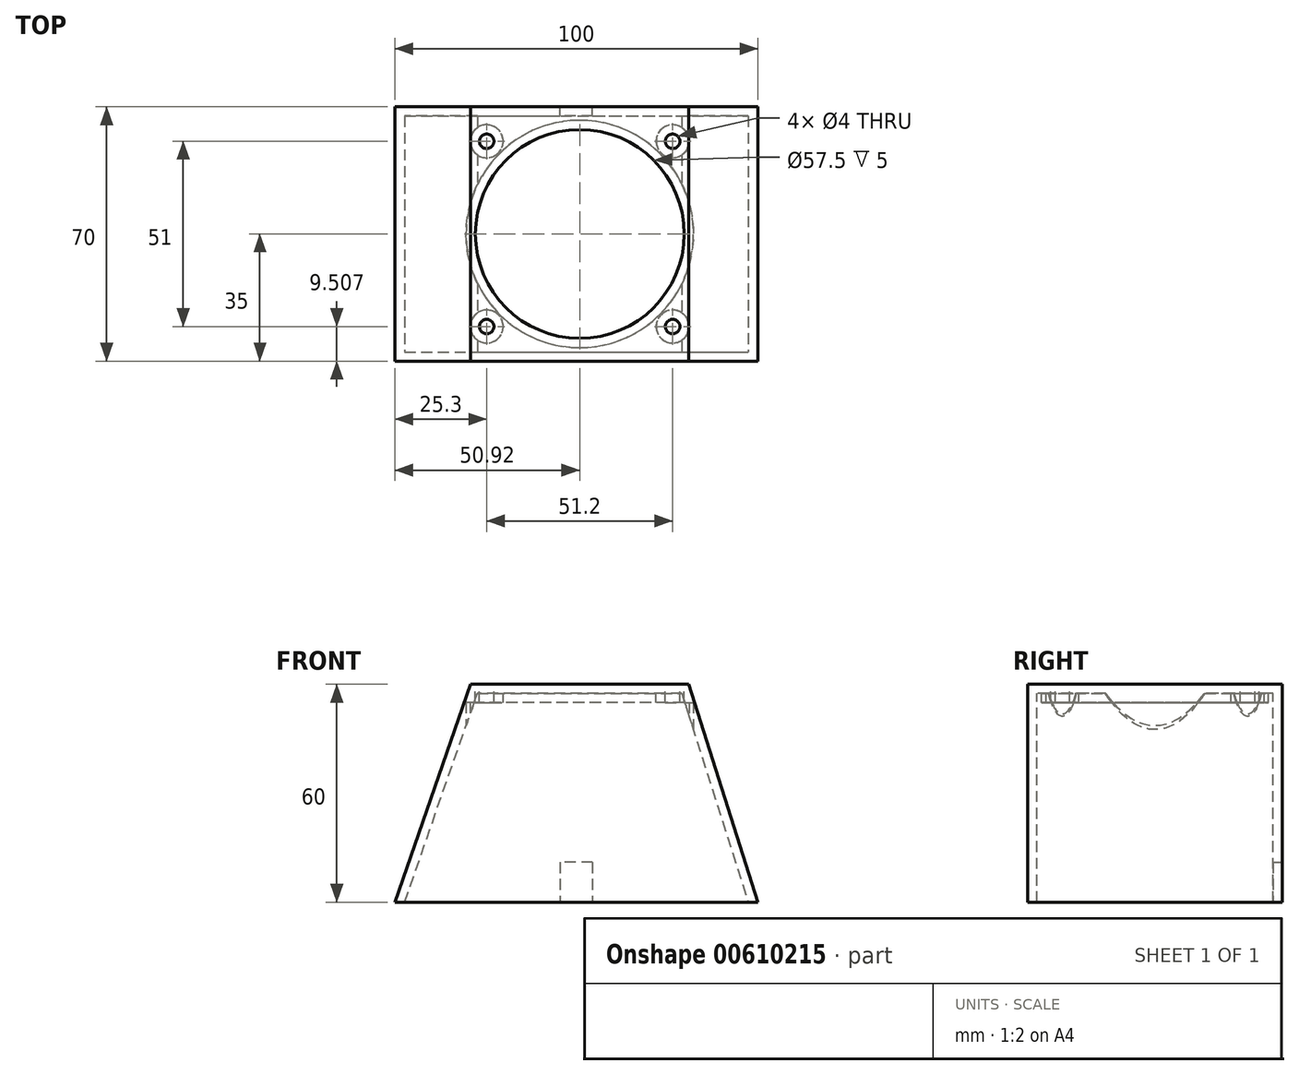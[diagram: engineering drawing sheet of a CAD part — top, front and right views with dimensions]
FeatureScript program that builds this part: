
annotation { "Feature Type Name" : "Feature", "Feature Type Description" : "" }
export const myFeature = defineFeature(function(context is Context, id is Id, definition is map)
    precondition{}
    {
        {
            var Q0;
            Q0=qCreatedBy(makeId("Top.planeOp"),FACE);
            var sketch = newSketch(context, id + "F0", { "sketchPlane" : qUnion([Q0])});
            skLineSegment(sketch, "E0.bottom", {"start": v(-50, 35) * mm, "end": v(50, 35) * mm});
            skLineSegment(sketch, "E0.top", {"start": v(-50, -35) * mm, "end": v(50, -35) * mm});
            skLineSegment(sketch, "E0.left", {"start": v(-50, 35) * mm, "end": v(-50, -35) * mm});
            skLineSegment(sketch, "E0.right", {"start": v(50, 35) * mm, "end": v(50, -35) * mm});
            skPoint(sketch, "E0.middle", {"position": v(0, 0) * mm});
            skSolve(sketch);
        }
        {
            var Q0;
            Q0 = qSketchRegion(id + "F0", true);
            extrude(context, id + "F1", {"entities" : qUnion([Q0]), "depth" : 60 * mm, "offsetDistance" : 25.4 * mm});
        }
        {
            var Q0;
            Q0=makeQuery(id+"F1.opExtrude","SWEPT_FACE",FACE,{"disambiguationData":[OSD([sQuery(id+"F0.wireOp",EDGE,"E0.top")])]});
            var sketch = newSketch(context, id + "F2", { "sketchPlane" : qUnion([Q0])});
            skLineSegment(sketch, "E1", {"start": v(-50, 0) * mm, "end": v(-29.1, 60) * mm});
            skLineSegment(sketch, "E2", {"start": v(-29.1, 60) * mm, "end": v(30.9, 60) * mm});
            skLineSegment(sketch, "E3", {"start": v(30.9, 60) * mm, "end": v(50, 0) * mm});
            skLineSegment(sketch, "E4", {"start": v(-50, 0) * mm, "end": v(-50, 60) * mm});
            skLineSegment(sketch, "E5", {"start": v(-50, 60) * mm, "end": v(-29.1, 60) * mm});
            skLineSegment(sketch, "E6", {"start": v(50, 60) * mm, "end": v(50, 0) * mm});
            skLineSegment(sketch, "E7", {"start": v(50, 60) * mm, "end": v(30.9, 60) * mm});
            skSolve(sketch);
        }
        {
            var Q0;
            Q0=makeQuery(id+"F2.imprint","IMPRINT",FACE,{"disambiguationData":[TD([[makeQuery(id+"F2.imprint","IMPRINT",EDGE,{"derivedFrom":sQuery(id+"F2.wireOp",EDGE,"E1")}),1.0]])]});
            var Q1;
            Q1=makeQuery(id+"F2.imprint","IMPRINT",FACE,{"disambiguationData":[TD([[makeQuery(id+"F2.imprint","IMPRINT",EDGE,{"derivedFrom":sQuery(id+"F2.wireOp",EDGE,"E3")}),1.0]])]});
            extrude(context, id + "F3", {"entities" : qUnion([Q0, Q1]), "operationType" : NewBodyOperationType.REMOVE, "endBound" : BoundingType.THROUGH_ALL, "oppositeDirection" : true, "depth" : 25.4 * mm, "offsetDistance" : 25.4 * mm});
        }
        {
            var Q0;
            Q0=makeQuery(id+"F1.opExtrude","CAP_FACE",FACE,{"disambiguationData":[OSD([sQuery(id+"F0.wireOp",EDGE,"E0.bottom"),sQuery(id+"F0.wireOp",EDGE,"E0.top"),sQuery(id+"F0.wireOp",EDGE,"E0.left"),sQuery(id+"F0.wireOp",EDGE,"E0.right")])],"isStart":false});
            var sketch = newSketch(context, id + "F4", { "sketchPlane" : qUnion([Q0])});
            skCircle(sketch, "E8", {"center": v(-24.7, 25.5) * mm, "radius": 2 * mm});
            skCircle(sketch, "E9", {"center": v(26.5, 25.5) * mm, "radius": 2 * mm});
            skCircle(sketch, "E10", {"center": v(26.5, -25.5) * mm, "radius": 2 * mm});
            skCircle(sketch, "E11", {"center": v(-24.7, -25.5) * mm, "radius": 2 * mm});
            skSolve(sketch);
        }
        {
            var Q0;
            Q0 = qSketchRegion(id + "F4", true);
            extrude(context, id + "F5", {"entities" : qUnion([Q0]), "operationType" : NewBodyOperationType.REMOVE, "endBound" : BoundingType.THROUGH_ALL, "oppositeDirection" : true, "depth" : 25.4 * mm, "offsetDistance" : 25.4 * mm});
        }
        {
            var Q0;
            Q0=makeQuery(id+"F1.opExtrude","CAP_FACE",FACE,{"disambiguationData":[OSD([sQuery(id+"F0.wireOp",EDGE,"E0.bottom"),sQuery(id+"F0.wireOp",EDGE,"E0.top"),sQuery(id+"F0.wireOp",EDGE,"E0.left"),sQuery(id+"F0.wireOp",EDGE,"E0.right")])],"isStart":false});
            var sketch = newSketch(context, id + "F6", { "sketchPlane" : qUnion([Q0])});
            skCircle(sketch, "E12", {"center": v(0.92, 0) * mm, "radius": 28.75 * mm});
            skSolve(sketch);
        }
        {
            var Q0;
            {var subQ0=sQuery(id+"F6.wireOp",EDGE,"E12");var subQ1=sQuery(id+"F2.wireOp",EDGE,"E2");var subQ2=makeQuery(id+"F6.imprint","INTERSECT",VERTEX,{"derivedFrom":[makeQuery(id+"F3.boolean.opBoolean","COPY",EDGE,{"derivedFrom":makeQuery(id+"F3.opExtrude","SWEPT_EDGE",EDGE,{"disambiguationData":[OSD([sQuery(id+"F2.wireOp",EDGE,"E1"),subQ1,sQuery(id+"F2.wireOp",EDGE,"E5")])]})}),subQ0]});Q0=makeQuery(id+"F6.imprint","IMPRINT",FACE,{"disambiguationData":[TD([[makeQuery(id+"F6.imprint","IMPRINT",EDGE,{"disambiguationData":[TD([[subQ2,1.0]])],"derivedFrom":subQ0}),1.0]])]});}
            extrude(context, id + "F7", {"entities" : qUnion([Q0]), "operationType" : NewBodyOperationType.REMOVE, "endBound" : BoundingType.THROUGH_ALL, "oppositeDirection" : true, "depth" : 25.4 * mm, "offsetDistance" : 25.4 * mm});
        }
        {
            var Q0;
            Q0=makeQuery(id+"F1.opExtrude","CAP_FACE",FACE,{"disambiguationData":[OSD([sQuery(id+"F0.wireOp",EDGE,"E0.bottom"),sQuery(id+"F0.wireOp",EDGE,"E0.top"),sQuery(id+"F0.wireOp",EDGE,"E0.left"),sQuery(id+"F0.wireOp",EDGE,"E0.right")])],"isStart":true});
            shell(context, id + "F8", {"entities" : qUnion([Q0]), "thickness" : 2.54 * mm});
        }
        {
            var Q0;
            {var subQ0=sQuery(id+"F0.wireOp",EDGE,"E0.right");var subQ1=sQuery(id+"F0.wireOp",EDGE,"E0.left");var subQ2=sQuery(id+"F0.wireOp",EDGE,"E0.top");var subQ3=sQuery(id+"F0.wireOp",EDGE,"E0.bottom");Q0=makeQuery(id+"F8.opShell","OFFSET_FACE",FACE,{"disambiguationData":[OSD([subQ3,subQ2,subQ1,subQ0]),TDD([makeQuery(id+"F1.opExtrude","CAP_FACE",FACE,{"disambiguationData":[OSD([subQ3,subQ2,subQ1,subQ0])],"isStart":true})]),OD(4.0)]});}
            var sketch = newSketch(context, id + "F9", { "sketchPlane" : qUnion([Q0])});
            skCircle(sketch, "E13.0.0", {"center": v(0.92, 0) * mm, "radius": 31.29 * mm});
            skCircle(sketch, "E14.0", {"center": v(0.92, 0) * mm, "radius": 28.75 * mm});
            skCircle(sketch, "E15.0", {"center": v(-24.7, 25.5) * mm, "radius": 4.54 * mm});
            skCircle(sketch, "E16.0", {"center": v(-24.7, 25.5) * mm, "radius": 2 * mm});
            skCircle(sketch, "E17.0", {"center": v(26.5, 25.5) * mm, "radius": 2 * mm});
            skCircle(sketch, "E18.0", {"center": v(26.5, 25.5) * mm, "radius": 4.54 * mm});
            skCircle(sketch, "E19.0", {"center": v(26.5, -25.5) * mm, "radius": 4.54 * mm});
            skCircle(sketch, "E20.0", {"center": v(26.5, -25.5) * mm, "radius": 2 * mm});
            skCircle(sketch, "E21.0", {"center": v(-24.7, -25.5) * mm, "radius": 2 * mm});
            skCircle(sketch, "E22.0", {"center": v(-24.7, -25.5) * mm, "radius": 4.54 * mm});
            skSolve(sketch);
        }
        {
            var Q0;
            Q0 = qSketchRegion(id + "F9", true);
            extrude(context, id + "F10", {"entities" : qUnion([Q0]), "operationType" : NewBodyOperationType.REMOVE, "oppositeDirection" : true, "depth" : 55 * mm, "offsetDistance" : 25.4 * mm});
        }
        {
            var Q0;
            Q0=makeQuery(id+"F1.opExtrude","SWEPT_FACE",FACE,{"disambiguationData":[OSD([sQuery(id+"F0.wireOp",EDGE,"E0.bottom")])]});
            var sketch = newSketch(context, id + "F11", { "sketchPlane" : qUnion([Q0])});
            skLineSegment(sketch, "E23.bottom", {"start": v(-4.4, 11) * mm, "end": v(4.5, 11) * mm});
            skLineSegment(sketch, "E23.top", {"start": v(-4.4, 0) * mm, "end": v(4.5, 0) * mm});
            skLineSegment(sketch, "E23.left", {"start": v(-4.4, 11) * mm, "end": v(-4.4, 0) * mm});
            skLineSegment(sketch, "E23.right", {"start": v(4.5, 11) * mm, "end": v(4.5, 0) * mm});
            skSolve(sketch);
        }
        {
            var Q0;
            Q0=makeQuery(id+"F11.imprint","IMPRINT",FACE,{"disambiguationData":[TD([[makeQuery(id+"F11.imprint","IMPRINT",EDGE,{"derivedFrom":sQuery(id+"F11.wireOp",EDGE,"E23.bottom")}),-1.0]])]});
            extrude(context, id + "F12", {"entities" : qUnion([Q0]), "operationType" : NewBodyOperationType.REMOVE, "oppositeDirection" : true, "depth" : 25.4 * mm, "offsetDistance" : 25.4 * mm});
        }
    });
